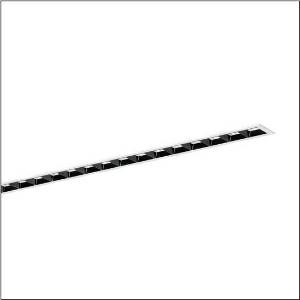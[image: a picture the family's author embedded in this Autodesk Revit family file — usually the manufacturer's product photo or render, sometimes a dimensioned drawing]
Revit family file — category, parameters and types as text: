
# Revit family: silica_21_51mx12tctaw
name_source: partatom
category: Lighting Fixtures
units: mm (PartAtom-declared; Revit-internal decimal feet)

## family parameters
Cut with Voids When Loaded = No
Host = Face
Light Source = No
Part Type = Normal
Room Calculation Point = No
Round Connector Dimension = Use Diameter
Shared = No

## types (1)
- --- (1 x LED, 9300 lm, 80.4 W, 6500K)
    Apparent Load = 80 VA
    CIE Flux Codes = 84 100 100 100 100
    Color Rendering = 80
    Color Temperature = 6500K
    Default Elevation = 1800 mm
    Description = Silica 21, office luminaire, primary light control with darklight reflector, of PMMA, black, CAT 2 (L<= 3000cd/m²), light emission: direct distribution, primary light characteristic: symmetric, installation type: recessed, LED, rated luminous flux: 9.300lm, luminous efficacy: 110lm/W, light colour: 8tw, colour temperature: 2700..6500K, control gear: DALI DT8, with terminal, 3+2-pole, max. 2.5mm², mains connection: 220..240V, AC, 50/60Hz, rated input power: 84.5W, luminaire housing, of aluminium, traffic white (RAL 9016), length: 3.028mm, width: 79mm, height: 53mm, protection rating (complete): IP20, insulation class (complete): insulation class I (protective earthing), certification: CE, ENEC, VDE, permissible operating ambient temperature: 0..+35°C, standard: EN 50419, packaging unit: 1 piece
    Height = 0 mm  [stored 0 ft]
    Lamp = 1 x LED
    Lamp Light Flux = 9300 lm
    Lamp Power = 80.4 W
    Lamp count = 1
    Length = 3027 mm
    Luminous efficacy = 116 lm/W
    Manufacturer = Siteco
    ModVariant = No
    Model = 51MX12TCTAW
    Mounting Place = Ceiling
    Mounting Type = Recessed
    Number of Poles = 1
    OnlyDefault = Yes
    Power Factor = 1
    Product Name = Silica 21
    Product group = office luminaire | ceiling recessed
    ProductGroupID = 400
    Protection Class = Protection class I
    Protection Degree = IP 20
    RLX_Detail_Level = 1
    RLX_Emergency_Light_Flux = 0 lm
    RLX_Emergency_Type = 0
    RLX_Emergency_Type_DB = No
    RlxData = <blob elided: 60225 chars, md5=2880dc38>
    Socket = socket
    Standby Power = 0 W
    System Light Flux = 9300 lm
    System Power = 80 W
    Type Comments = individual setting
    Type Image = l_1335880.jpg
    URL = http://relux.com
    VarID = @adj_139661
    Voltage = 0 V
    Weight = 0.00 kg
    Width = 79 mm

note: [stored X ft] marks values corroborated as IEEE doubles in the binary element streams (Revit-internal decimal feet)

## geometry (parser evidence)
native form markers: Blend x4, Sweep x11
no freeform markers — native parametric forms only
